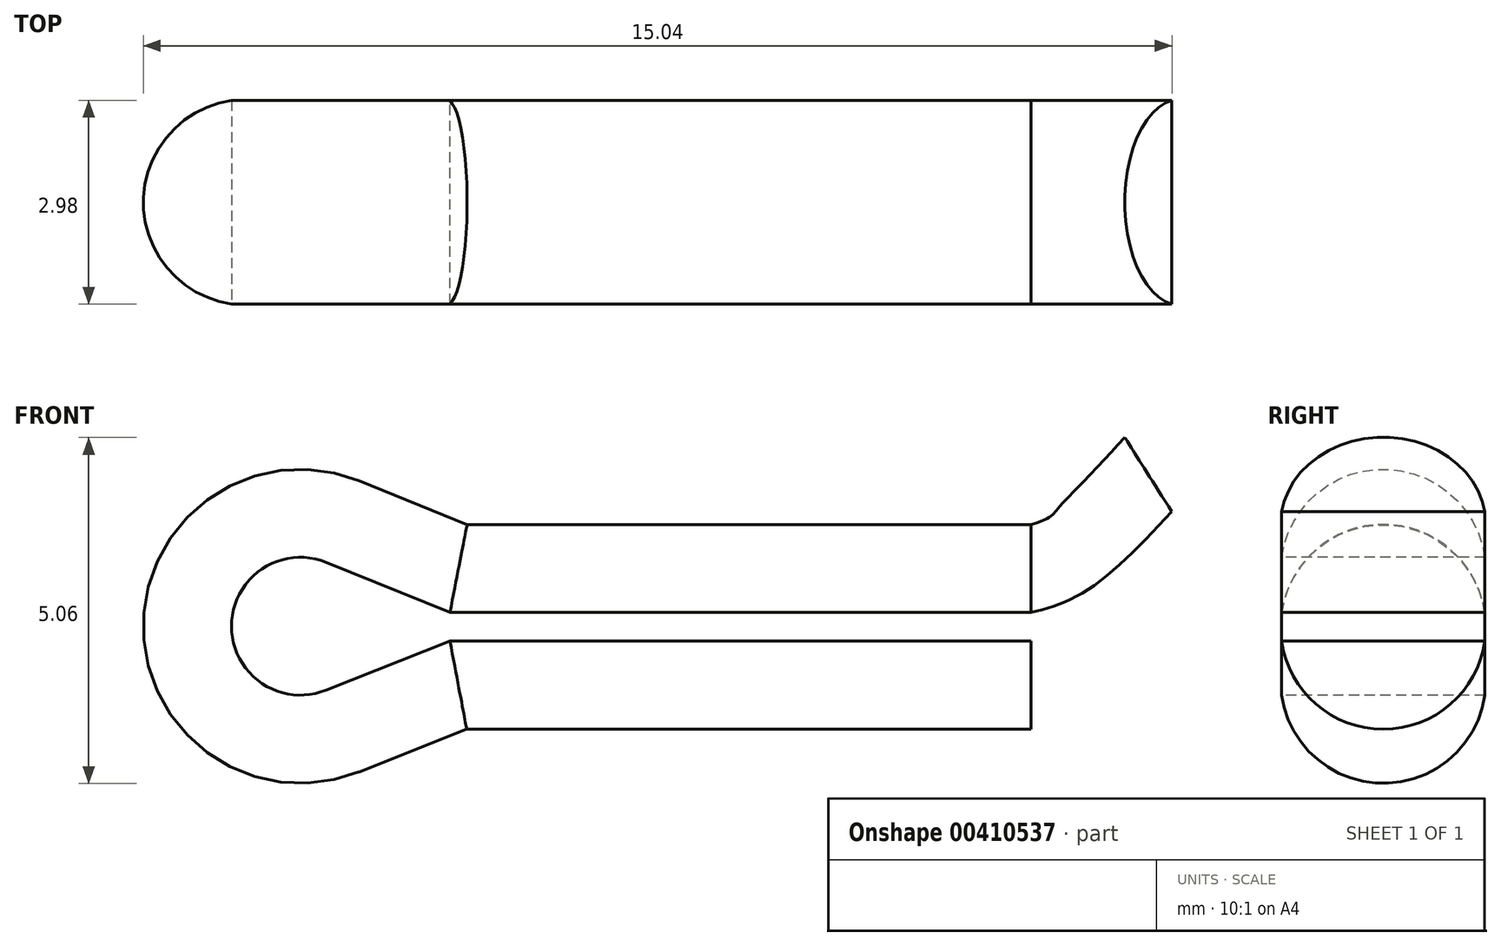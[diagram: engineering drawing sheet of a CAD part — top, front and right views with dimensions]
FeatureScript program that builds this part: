
annotation { "Feature Type Name" : "Feature", "Feature Type Description" : "" }
export const myFeature = defineFeature(function(context is Context, id is Id, definition is map)
    precondition{}
    {
        {
            var Q0;
            Q0=qCreatedBy(makeId("Right.planeOp"),FACE);
            var sketch = newSketch(context, id + "F0", { "sketchPlane" : qUnion([Q0])});
            skCircle(sketch, "E0", {"center": v(0, 0) * mm, "radius": 1.5 * mm, "construction": true});
            skLineSegment(sketch, "E1.bottom", {"start": v(-1.94, 0.2) * mm, "end": v(1.94, 0.2) * mm, "construction": true});
            skLineSegment(sketch, "E1.top", {"start": v(-1.94, -0.2) * mm, "end": v(1.94, -0.2) * mm, "construction": true});
            skLineSegment(sketch, "E1.left", {"start": v(-1.94, 0.2) * mm, "end": v(-1.94, -0.2) * mm, "construction": true});
            skLineSegment(sketch, "E1.right", {"start": v(1.94, 0.2) * mm, "end": v(1.94, -0.2) * mm, "construction": true});
            skArc(sketch, "E2", {"start": v(1.49, 0.2) * mm, "mid": v(0, 1.49) * mm, "end": v(-1.49, 0.2) * mm});
            skLineSegment(sketch, "E3", {"start": v(-1.49, 0.2) * mm, "end": v(1.49, 0.2) * mm});
            skSolve(sketch);
        }
        {
            var Q0;
            Q0=qCreatedBy(makeId("Front.planeOp"),FACE);
            var sketch = newSketch(context, id + "F1", { "sketchPlane" : qUnion([Q0])});
            skLineSegment(sketch, "E4", {"start": v(0, 0.2) * mm, "end": v(-8.5, 0.2) * mm});
            skLineSegment(sketch, "E5", {"start": v(-8.5, 0.2) * mm, "end": v(-10.31, 0.93) * mm});
            skArc(sketch, "E6", {"start": v(-10.31, 0.93) * mm, "mid": v(-11.69, 0) * mm, "end": v(-10.31, -0.93) * mm});
            skLineSegment(sketch, "E7", {"start": v(-8.5, -0.21) * mm, "end": v(0, -0.21) * mm});
            skLineSegment(sketch, "E8.0", {"start": v(0, 1.5) * mm, "end": v(0, -1.5) * mm});
            skLineSegment(sketch, "E9", {"start": v(0, -0.21) * mm, "end": v(0, -0.21) * mm});
            skLineSegment(sketch, "E10", {"start": v(-10.31, -0.93) * mm, "end": v(-8.5, -0.21) * mm});
            skLineSegment(sketch, "E11", {"start": v(-8.5, 4.74) * mm, "end": v(-8.5, -4.35) * mm, "construction": true});
            skFitSpline(sketch, "E12", {"points": [v(0, 0.2) * mm, v(0.8, 0.5) * mm, v(2.06, 1.67) * mm], "startDerivative": vector(1.87, 0.5) * mm, "endDerivative": vector(2.2, 2.35) * mm});
            skFitSpline(sketch, "E13", {"points": [v(0, -0.21) * mm, v(0.33, -0.28) * mm, v(0.85, -0.6) * mm, v(1.94, -1.64) * mm], "startDerivative": vector(1.9, -0.05) * mm, "endDerivative": vector(0.27, -0.55) * mm});
            skSolve(sketch);
        }
        {
            var Q0;
            Q0=makeQuery(id+"F0.imprint","IMPRINT",FACE,{"disambiguationData":[TD([[makeQuery(id+"F0.imprint","IMPRINT",EDGE,{"derivedFrom":sQuery(id+"F0.wireOp",EDGE,"E2")}),1.0]])]});
            var Q1;
            Q1=sQuery(id+"F1.wireOp",EDGE,"E4");
            var Q2;
            Q2=sQuery(id+"F1.wireOp",EDGE,"E5");
            var Q3;
            Q3=sQuery(id+"F1.wireOp",EDGE,"E6");
            var Q4;
            Q4=sQuery(id+"F1.wireOp",EDGE,"E10");
            var Q5;
            Q5=sQuery(id+"F1.wireOp",EDGE,"E7");
            sweep(context, id + "F2", {"profiles" : qUnion([Q0]), "path" : qUnion([Q1, Q2, Q3, Q4, Q5])});
        }
        {
            var Q0;
            Q0=makeQuery(id+"F0.imprint","IMPRINT",FACE,{"disambiguationData":[TD([[makeQuery(id+"F0.imprint","IMPRINT",EDGE,{"derivedFrom":sQuery(id+"F0.wireOp",EDGE,"E2")}),1.0]])]});
            var Q1;
            Q1=sQuery(id+"F1.wireOp",EDGE,"E12");
            sweep(context, id + "F3", {"operationType" : NewBodyOperationType.ADD, "profiles" : qUnion([Q0]), "path" : qUnion([Q1])});
        }
    });
